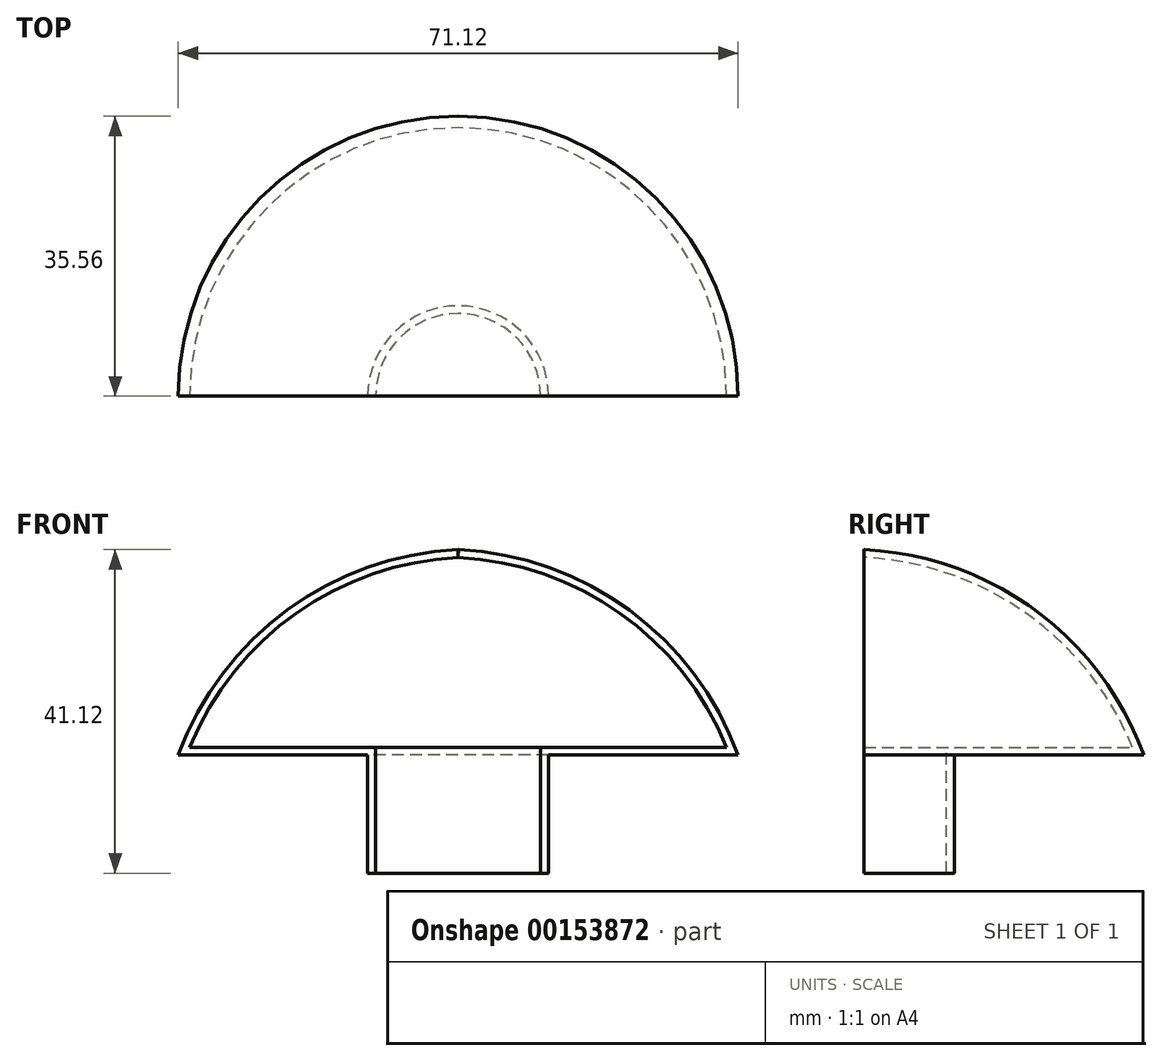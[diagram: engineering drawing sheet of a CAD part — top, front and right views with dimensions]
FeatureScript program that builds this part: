
annotation { "Feature Type Name" : "Feature", "Feature Type Description" : "" }
export const myFeature = defineFeature(function(context is Context, id is Id, definition is map)
    precondition{}
    {
        {
            var Q0;
            Q0=qCreatedBy(makeId("Front.planeOp"),FACE);
            var sketch = newSketch(context, id + "F0", { "sketchPlane" : qUnion([Q0])});
            skArc(sketch, "E0", {"start": v(0, 24.1) * mm, "mid": v(-20.56, 17.02) * mm, "end": v(-34.1, 0) * mm});
            skArc(sketch, "E1.0", {"start": v(-0.05, 25.1) * mm, "mid": v(-21.74, 17.4) * mm, "end": v(-35.56, -1) * mm});
            skLineSegment(sketch, "E2", {"start": v(-34.1, 0) * mm, "end": v(-10.48, 0) * mm});
            skLineSegment(sketch, "E3", {"start": v(-10.48, 0) * mm, "end": v(-10.48, -16.02) * mm});
            skLineSegment(sketch, "E4", {"start": v(-10.48, -16.02) * mm, "end": v(-11.48, -16.02) * mm});
            skLineSegment(sketch, "E5", {"start": v(-11.48, -16.02) * mm, "end": v(-11.48, -1) * mm});
            skLineSegment(sketch, "E6", {"start": v(-11.48, -1) * mm, "end": v(-35.56, -1) * mm});
            skLineSegment(sketch, "E7", {"start": v(-0.05, 25.1) * mm, "end": v(0, 24.1) * mm});
            skLineSegment(sketch, "E8", {"start": v(0, 30.5) * mm, "end": v(0, -19.9) * mm, "construction": true});
            skSolve(sketch);
        }
        {
            var Q0;
            Q0=makeQuery(id+"F0.imprint","IMPRINT",FACE,{"disambiguationData":[TD([[makeQuery(id+"F0.imprint","IMPRINT",EDGE,{"derivedFrom":sQuery(id+"F0.wireOp",EDGE,"E0")}),-1.0]])]});
            var Q1;
            Q1=sQuery(id+"F0.wireOp",EDGE,"E8");
            var Q2;
            Q2=sQuery(id+"F0.wireOp",EDGE,"E8");
            revolve(context, id + "F1", {"entities" : qUnion([Q0]), "surfaceEntities" : qUnion([Q1]), "axis" : qUnion([Q2]), "revolveType" : RevolveType.ONE_DIRECTION, "angle" : 180 * degree});
        }
    });
